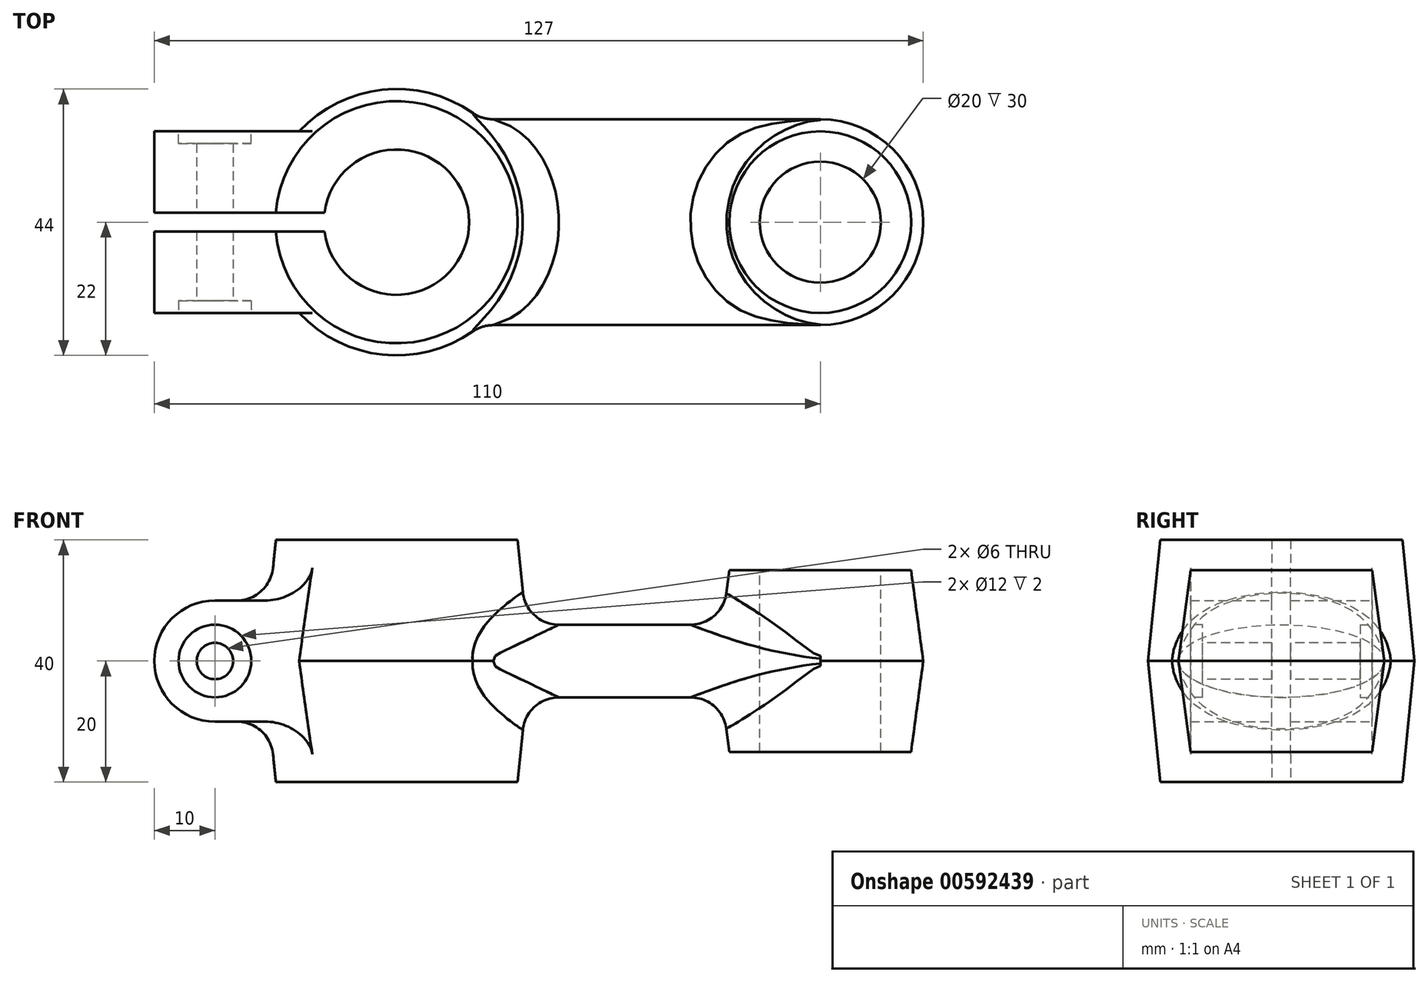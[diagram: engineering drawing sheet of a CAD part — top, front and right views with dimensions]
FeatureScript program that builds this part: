
annotation { "Feature Type Name" : "Feature", "Feature Type Description" : "" }
export const myFeature = defineFeature(function(context is Context, id is Id, definition is map)
    precondition{}
    {
        {
            var Q0;
            Q0=qCreatedBy(makeId("Front.planeOp"),FACE);
            var sketch = newSketch(context, id + "F0", { "sketchPlane" : qUnion([Q0])});
            skLineSegment(sketch, "E0", {"start": v(0, 20) * mm, "end": v(0, -20) * mm});
            skLineSegment(sketch, "E1", {"start": v(0, 20) * mm, "end": v(20, 20) * mm});
            skLineSegment(sketch, "E2", {"start": v(20, 20) * mm, "end": v(22, 0) * mm});
            skLineSegment(sketch, "E3", {"start": v(22, 0) * mm, "end": v(20, -20) * mm});
            skLineSegment(sketch, "E4", {"start": v(0, -20) * mm, "end": v(20, -20) * mm});
            skSolve(sketch);
        }
        {
            var Q0;
            Q0 = qSketchRegion(id + "F0", true);
            var Q1;
            Q1=sQuery(id+"F0.wireOp",EDGE,"E0");
            revolve(context, id + "F1", {"entities" : qUnion([Q0]), "axis" : qUnion([Q1]), "revolveType" : RevolveType.FULL});
        }
        {
            var Q0;
            Q0=qCreatedBy(makeId("Front.planeOp"),FACE);
            var sketch = newSketch(context, id + "F2", { "sketchPlane" : qUnion([Q0])});
            skLineSegment(sketch, "E5", {"start": v(70, 15) * mm, "end": v(85, 15) * mm});
            skLineSegment(sketch, "E6", {"start": v(70, -15) * mm, "end": v(85, -15) * mm});
            skLineSegment(sketch, "E7", {"start": v(85, -15) * mm, "end": v(87, 0) * mm});
            skLineSegment(sketch, "E8", {"start": v(70, 15) * mm, "end": v(70, -15) * mm});
            skLineSegment(sketch, "E9", {"start": v(85, 15) * mm, "end": v(87, 0) * mm});
            skSolve(sketch);
        }
        {
            var Q0;
            Q0=makeQuery(id+"F2.imprint","IMPRINT",FACE,{"disambiguationData":[TD([[makeQuery(id+"F2.imprint","IMPRINT",EDGE,{"derivedFrom":sQuery(id+"F2.wireOp",EDGE,"E5")}),-1.0]])]});
            var Q1;
            Q1=sQuery(id+"F2.wireOp",EDGE,"E8");
            revolve(context, id + "F3", {"entities" : qUnion([Q0]), "axis" : qUnion([Q1]), "revolveType" : RevolveType.FULL});
        }
        {
            var Q0;
            Q0=qCreatedBy(makeId("Right.planeOp"),FACE);
            cPlane(context, id + "F4", {"entities" : qUnion([Q0]), "cplaneType" : CPlaneType.OFFSET, "offset" : 35 * mm, "width" : 150 * mm, "height" : 150 * mm});
        }
        {
            var Q0;
            Q0=qCreatedBy(id+"F4.planeOp",FACE);
            var sketch = newSketch(context, id + "F5", { "sketchPlane" : qUnion([Q0])});
            skEllipse(sketch, "E10", {"center": v(0, 0) * mm, "majorRadius": 17 * mm, "minorRadius": 6 * mm, "majorAxis": v(1, 0)});
            skSolve(sketch);
        }
        {
            var Q0;
            Q0 = qSketchRegion(id + "F5", true);
            extrude(context, id + "F6", {"entities" : qUnion([Q0]), "operationType" : NewBodyOperationType.ADD, "endBound" : BoundingType.SYMMETRIC, "depth" : 70 * mm, "offsetDistance" : 25 * mm});
        }
        {
            var Q0;
            Q0=makeQuery(id+"F6.boolean.opBoolean","INTERSECT",EDGE,{"derivedFrom":[makeQuery(id+"F1.opRevolve","SWEPT_FACE",FACE,{"disambiguationData":[OSD([sQuery(id+"F0.wireOp",EDGE,"E2")])]}),makeQuery(id+"F6.opExtrude","SWEPT_FACE",FACE,{"disambiguationData":[OSD([sQuery(id+"F5.wireOp",EDGE,"E10")])]})]});
            var Q1;
            Q1=makeQuery(id+"F6.boolean.opBoolean","INTERSECT",EDGE,{"derivedFrom":[makeQuery(id+"F1.opRevolve","SWEPT_FACE",FACE,{"disambiguationData":[OSD([sQuery(id+"F0.wireOp",EDGE,"E3")])]}),makeQuery(id+"F6.opExtrude","SWEPT_FACE",FACE,{"disambiguationData":[OSD([sQuery(id+"F5.wireOp",EDGE,"E10")])]})]});
            var Q2;
            Q2=makeQuery(id+"F6.boolean.opBoolean","INTERSECT",EDGE,{"derivedFrom":[makeQuery(id+"F3.opRevolve","SWEPT_FACE",FACE,{"disambiguationData":[OSD([sQuery(id+"F2.wireOp",EDGE,"E7")])]}),makeQuery(id+"F6.opExtrude","SWEPT_FACE",FACE,{"disambiguationData":[OSD([sQuery(id+"F5.wireOp",EDGE,"E10")])]})]});
            var Q3;
            Q3=makeQuery(id+"F6.boolean.opBoolean","INTERSECT",EDGE,{"derivedFrom":[makeQuery(id+"F3.opRevolve","SWEPT_FACE",FACE,{"disambiguationData":[OSD([sQuery(id+"F2.wireOp",EDGE,"E9")])]}),makeQuery(id+"F6.opExtrude","SWEPT_FACE",FACE,{"disambiguationData":[OSD([sQuery(id+"F5.wireOp",EDGE,"E10")])]})]});
            fillet(context, id + "F7", {"entities" : qUnion([Q0, Q1, Q2, Q3]), "radius" : 6 * mm, "tangentPropagation" : true, "allowEdgeOverflow" : false});
        }
        {
            var Q0;
            Q0=makeQuery(id+"F1.opRevolve","SWEPT_FACE",FACE,{"disambiguationData":[OSD([sQuery(id+"F0.wireOp",EDGE,"E1")])]});
            var sketch = newSketch(context, id + "F8", { "sketchPlane" : qUnion([Q0])});
            skCircle(sketch, "E11", {"center": v(0, 0) * mm, "radius": 12 * mm});
            skCircle(sketch, "E12", {"center": v(70, 0) * mm, "radius": 10 * mm});
            skSolve(sketch);
        }
        {
            var Q0;
            Q0 = qSketchRegion(id + "F8", true);
            extrude(context, id + "F9", {"entities" : qUnion([Q0]), "operationType" : NewBodyOperationType.REMOVE, "endBound" : BoundingType.THROUGH_ALL, "oppositeDirection" : true, "depth" : 25 * mm, "offsetDistance" : 25 * mm});
        }
        {
            var Q0;
            Q0=qCreatedBy(makeId("Front.planeOp"),FACE);
            var sketch = newSketch(context, id + "F10", { "sketchPlane" : qUnion([Q0])});
            skLineSegment(sketch, "E13", {"start": v(0, -22.97) * mm, "end": v(0, 26.28) * mm, "construction": true});
            skLineSegment(sketch, "E14.0", {"start": v(-40, 0) * mm, "end": v(-40, 0) * mm});
            skLineSegment(sketch, "E15", {"start": v(0, 0) * mm, "end": v(-40, 0) * mm, "construction": true});
            skLineSegment(sketch, "E16.0", {"start": v(-14, 10) * mm, "end": v(-30, 10) * mm});
            skLineSegment(sketch, "E17.0", {"start": v(-14, -10) * mm, "end": v(-30, -10) * mm});
            skPoint(sketch, "E18.orphan", {"position": v(12, 10) * mm});
            skPoint(sketch, "E19.orphan", {"position": v(12, -10) * mm});
            skPoint(sketch, "E20.visualSharp", {"position": v(-40, 10) * mm});
            skArc(sketch, "E20.filletArc", {"start": v(-30, 10) * mm, "mid": v(-37.07, 7.07) * mm, "end": v(-40, 0) * mm});
            skPoint(sketch, "E21.visualSharp", {"position": v(-40, -10) * mm});
            skArc(sketch, "E21.filletArc", {"start": v(-40, 0) * mm, "mid": v(-37.07, -7.07) * mm, "end": v(-30, -10) * mm});
            skLineSegment(sketch, "E22.0", {"start": v(-14, 10) * mm, "end": v(-14, -10) * mm});
            skSolve(sketch);
        }
        {
            var Q0;
            Q0 = qSketchRegion(id + "F10", true);
            extrude(context, id + "F11", {"entities" : qUnion([Q0]), "operationType" : NewBodyOperationType.ADD, "endBound" : BoundingType.SYMMETRIC, "depth" : 30 * mm, "offsetDistance" : 25 * mm});
        }
        {
            var Q0;
            Q0=makeQuery(id+"F11.opExtrude","CAP_FACE",FACE,{"disambiguationData":[OSD([sQuery(id+"F10.wireOp",EDGE,"E16.0"),sQuery(id+"F10.wireOp",EDGE,"E17.0"),sQuery(id+"F10.wireOp",EDGE,"E20.filletArc"),sQuery(id+"F10.wireOp",EDGE,"E21.filletArc"),sQuery(id+"F10.wireOp",EDGE,"E22.0")])],"isStart":false});
            var sketch = newSketch(context, id + "F12", { "sketchPlane" : qUnion([Q0])});
            skCircle(sketch, "E23", {"center": v(-30, 0) * mm, "radius": 3 * mm});
            skSolve(sketch);
        }
        {
            var Q0;
            Q0 = qSketchRegion(id + "F12", true);
            extrude(context, id + "F13", {"entities" : qUnion([Q0]), "operationType" : NewBodyOperationType.REMOVE, "endBound" : BoundingType.THROUGH_ALL, "oppositeDirection" : true, "depth" : 25 * mm, "offsetDistance" : 25 * mm});
        }
        {
            var Q0;
            Q0=makeQuery(id+"F11.opExtrude","CAP_FACE",FACE,{"disambiguationData":[OSD([sQuery(id+"F10.wireOp",EDGE,"E16.0"),sQuery(id+"F10.wireOp",EDGE,"E17.0"),sQuery(id+"F10.wireOp",EDGE,"E20.filletArc"),sQuery(id+"F10.wireOp",EDGE,"E21.filletArc"),sQuery(id+"F10.wireOp",EDGE,"E22.0")])],"isStart":false});
            var sketch = newSketch(context, id + "F14", { "sketchPlane" : qUnion([Q0])});
            skCircle(sketch, "E24", {"center": v(-30, 0) * mm, "radius": 6 * mm});
            skSolve(sketch);
        }
        {
            var Q0;
            Q0 = qSketchRegion(id + "F14", true);
            extrude(context, id + "F15", {"entities" : qUnion([Q0]), "operationType" : NewBodyOperationType.REMOVE, "oppositeDirection" : true, "depth" : 2 * mm, "offsetDistance" : 25 * mm});
        }
        {
            var Q0;
            Q0=makeQuery(id+"F11.boolean.opBoolean","INTERSECT",EDGE,{"derivedFrom":[makeQuery(id+"F1.opRevolve","SWEPT_FACE",FACE,{"disambiguationData":[OSD([sQuery(id+"F0.wireOp",EDGE,"E3")])]}),makeQuery(id+"F11.opExtrude","SWEPT_FACE",FACE,{"disambiguationData":[OSD([sQuery(id+"F10.wireOp",EDGE,"E17.0")])]})]});
            var Q1;
            Q1=makeQuery(id+"F11.boolean.opBoolean","INTERSECT",EDGE,{"derivedFrom":[makeQuery(id+"F1.opRevolve","SWEPT_FACE",FACE,{"disambiguationData":[OSD([sQuery(id+"F0.wireOp",EDGE,"E2")])]}),makeQuery(id+"F11.opExtrude","SWEPT_FACE",FACE,{"disambiguationData":[OSD([sQuery(id+"F10.wireOp",EDGE,"E16.0")])]})]});
            fillet(context, id + "F16", {"entities" : qUnion([Q0, Q1]), "radius" : 6 * mm, "tangentPropagation" : true, "allowEdgeOverflow" : false});
        }
        {
            var Q0;
            Q0=makeQuery(id+"F1.opRevolve","SWEPT_FACE",FACE,{"disambiguationData":[OSD([sQuery(id+"F0.wireOp",EDGE,"E1")])]});
            var sketch = newSketch(context, id + "F17", { "sketchPlane" : qUnion([Q0])});
            skLineSegment(sketch, "E25.0", {"start": v(-8, 1.56) * mm, "end": v(-44.86, 1.56) * mm});
            skLineSegment(sketch, "E26.0", {"start": v(-8, -1.56) * mm, "end": v(-44.86, -1.56) * mm});
            skLineSegment(sketch, "E27", {"start": v(-44.86, -1.56) * mm, "end": v(-44.86, 1.56) * mm});
            skLineSegment(sketch, "E28", {"start": v(-8, -1.56) * mm, "end": v(-8, 1.56) * mm});
            skSolve(sketch);
        }
        {
            var Q0;
            Q0 = qSketchRegion(id + "F17", true);
            extrude(context, id + "F18", {"entities" : qUnion([Q0]), "operationType" : NewBodyOperationType.REMOVE, "endBound" : BoundingType.THROUGH_ALL, "oppositeDirection" : true, "depth" : 25 * mm, "offsetDistance" : 25 * mm});
        }
        {
            var Q0;
            Q0=makeQuery(id+"F11.opExtrude","CAP_FACE",FACE,{"disambiguationData":[OSD([sQuery(id+"F10.wireOp",EDGE,"E16.0"),sQuery(id+"F10.wireOp",EDGE,"E17.0"),sQuery(id+"F10.wireOp",EDGE,"E20.filletArc"),sQuery(id+"F10.wireOp",EDGE,"E21.filletArc"),sQuery(id+"F10.wireOp",EDGE,"E22.0")])],"isStart":true});
            var sketch = newSketch(context, id + "F19", { "sketchPlane" : qUnion([Q0])});
            skCircle(sketch, "E29", {"center": v(30, 0) * mm, "radius": 6 * mm});
            skSolve(sketch);
        }
        {
            var Q0;
            Q0 = qSketchRegion(id + "F19", true);
            extrude(context, id + "F20", {"entities" : qUnion([Q0]), "operationType" : NewBodyOperationType.REMOVE, "oppositeDirection" : true, "depth" : 2 * mm, "offsetDistance" : 25 * mm});
        }
    });
